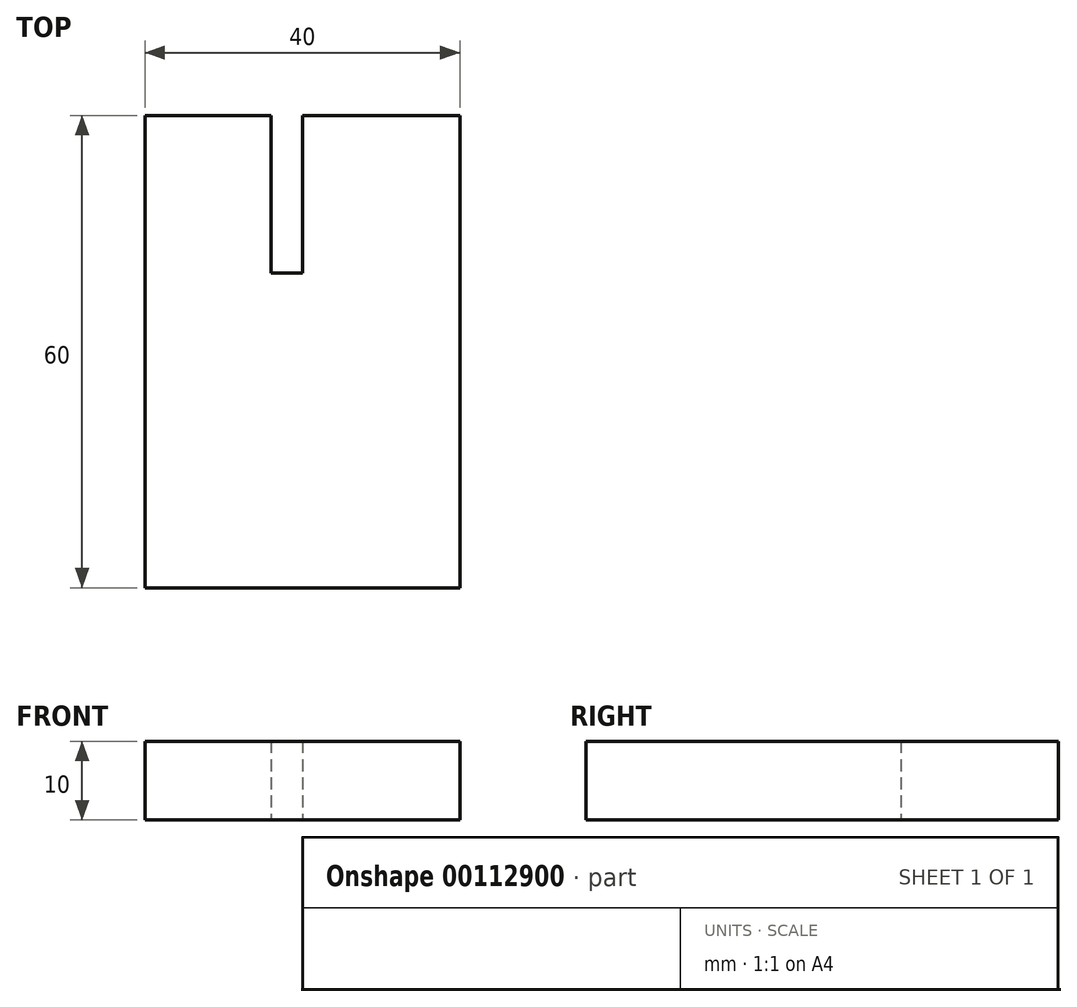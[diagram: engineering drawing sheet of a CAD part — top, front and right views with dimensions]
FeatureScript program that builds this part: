
annotation { "Feature Type Name" : "Feature", "Feature Type Description" : "" }
export const myFeature = defineFeature(function(context is Context, id is Id, definition is map)
    precondition{}
    {
        {
            var Q0;
            Q0=qCreatedBy(makeId("Top.planeOp"),FACE);
            var sketch = newSketch(context, id + "F0", { "sketchPlane" : qUnion([Q0])});
            skLineSegment(sketch, "E0.bottom", {"start": v(20, 30) * mm, "end": v(-20, 30) * mm});
            skLineSegment(sketch, "E0.top", {"start": v(20, -30) * mm, "end": v(-20, -30) * mm});
            skLineSegment(sketch, "E0.left", {"start": v(20, 30) * mm, "end": v(20, -30) * mm});
            skLineSegment(sketch, "E0.right", {"start": v(-20, 30) * mm, "end": v(-20, -30) * mm});
            skPoint(sketch, "E0.middle", {"position": v(0, 0) * mm});
            skLineSegment(sketch, "E1.bottom", {"start": v(0, 30) * mm, "end": v(-4, 30) * mm});
            skLineSegment(sketch, "E1.top", {"start": v(0, 10) * mm, "end": v(-4, 10) * mm});
            skLineSegment(sketch, "E1.left", {"start": v(0, 30) * mm, "end": v(0, 10) * mm});
            skLineSegment(sketch, "E1.right", {"start": v(-4, 30) * mm, "end": v(-4, 10) * mm});
            skLineSegment(sketch, "E2.MirrorCS", {"start": v(4, 30) * mm, "end": v(4, 10) * mm});
            skLineSegment(sketch, "E3.MirrorCS", {"start": v(0, 10) * mm, "end": v(4, 10) * mm});
            skSolve(sketch);
        }
        {
            var Q0;
            Q0=makeQuery(id+"F0.imprint","IMPRINT",FACE,{"disambiguationData":[TD([[makeQuery(id+"F0.imprint","IMPRINT",EDGE,{"derivedFrom":sQuery(id+"F0.wireOp",EDGE,"E0.top")}),-1.0]])]});
            var Q1;
            Q1=makeQuery(id+"F0.imprint","IMPRINT",FACE,{"disambiguationData":[TD([[makeQuery(id+"F0.imprint","IMPRINT",EDGE,{"derivedFrom":sQuery(id+"F0.wireOp",EDGE,"E1.bottom")}),1.0]])]});
            var Q2;
            {var subQ0=sQuery(id+"F0.wireOp",EDGE,"E1.left");Q2=makeQuery(id+"F0.imprint","IMPRINT",FACE,{"disambiguationData":[TD([[makeQuery(id+"F0.imprint","IMPRINT",EDGE,{"derivedFrom":subQ0}),1.0]])]});}
            extrude(context, id + "F1", {"entities" : qUnion([Q0, Q1, Q2]), "depth" : 10 * mm});
        }
    });
